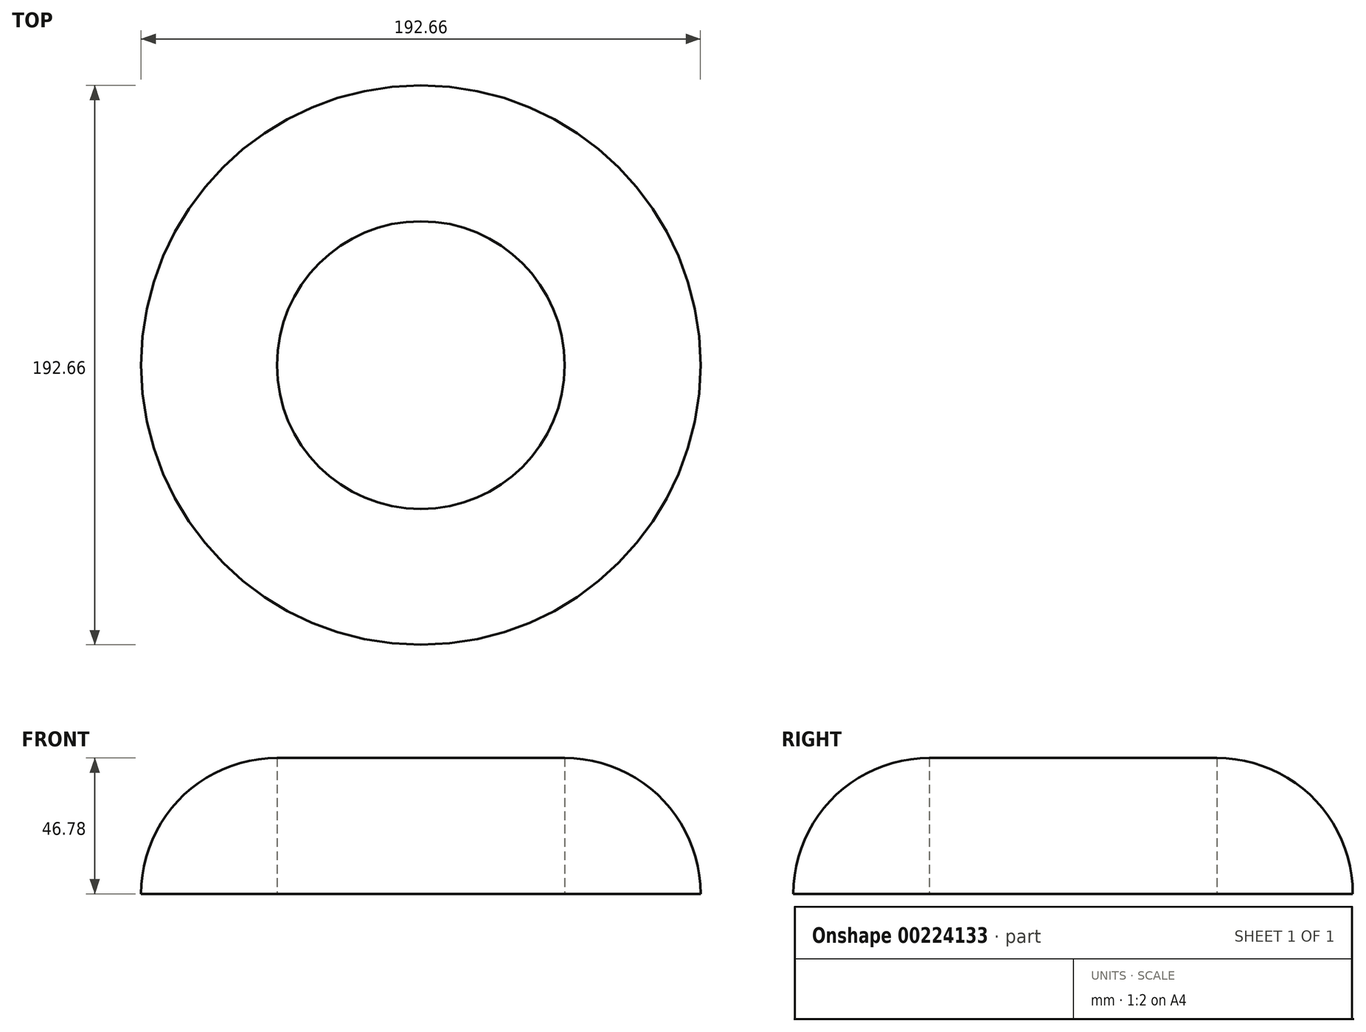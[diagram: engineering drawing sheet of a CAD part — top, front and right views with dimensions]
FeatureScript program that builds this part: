
annotation { "Feature Type Name" : "Feature", "Feature Type Description" : "" }
export const myFeature = defineFeature(function(context is Context, id is Id, definition is map)
    precondition{}
    {
        {
            var Q0;
            Q0=qCreatedBy(makeId("Front.planeOp"),FACE);
            var sketch = newSketch(context, id + "F0", { "sketchPlane" : qUnion([Q0])});
            skLineSegment(sketch, "E0", {"start": v(0, 46.78) * mm, "end": v(0, 0) * mm});
            skLineSegment(sketch, "E1", {"start": v(0, 0) * mm, "end": v(47.22, 0) * mm});
            skArc(sketch, "E2", {"start": v(0, 46.78) * mm, "mid": v(33.08, 33.08) * mm, "end": v(46.78, 0) * mm});
            skLineSegment(sketch, "E3", {"start": v(-49.55, 46.78) * mm, "end": v(-49.55, 0) * mm});
            skLineSegment(sketch, "E4", {"start": v(-49.55, 0) * mm, "end": v(-49.55, 46.78) * mm});
            skSolve(sketch);
        }
        {
            var Q0;
            {var subQ0=sQuery(id+"F0.wireOp",EDGE,"E0");Q0=makeQuery(id+"F0.imprint","IMPRINT",FACE,{"disambiguationData":[TD([[makeQuery(id+"F0.imprint","IMPRINT",EDGE,{"derivedFrom":subQ0}),1.0]])]});}
            var Q1;
            Q1=sQuery(id+"F0.wireOp",EDGE,"E4");
            revolve(context, id + "F1", {"entities" : qUnion([Q0]), "axis" : qUnion([Q1]), "revolveType" : RevolveType.FULL});
        }
    });
